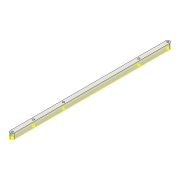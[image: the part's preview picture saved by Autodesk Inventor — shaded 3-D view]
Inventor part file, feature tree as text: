
AUTODESK INVENTOR PART (.ipt)
format: ipt  version: 2022 (Build 260153000, 153)  size: 102,912 bytes
history: native  units: mm
features: sketch x2, extrude x1, projected_geometry x1
ambient origin geometry x8: Origin, YZ Plane, XZ Plane, XY Plane, X Axis, Y Axis, Z Axis, Center Point
bodies: Solid1 (feature_tree)
feature tree (4):
  extrude  "Extrusion1"  Depth=6.0mm
  sketch  "Sketch2"  dims[d2=3.0mm d3=3.0mm d4=8.0mm d5=0.0mm d6=3.0mm d7=184.147mm d8=3.0mm d9=74.612mm d10=3.0mm d11=30.851mm]
  sketch  "Sketch1"  dims[d0=226.421mm d1=6.0mm]
  projected_geometry  "Projected Loop1"
